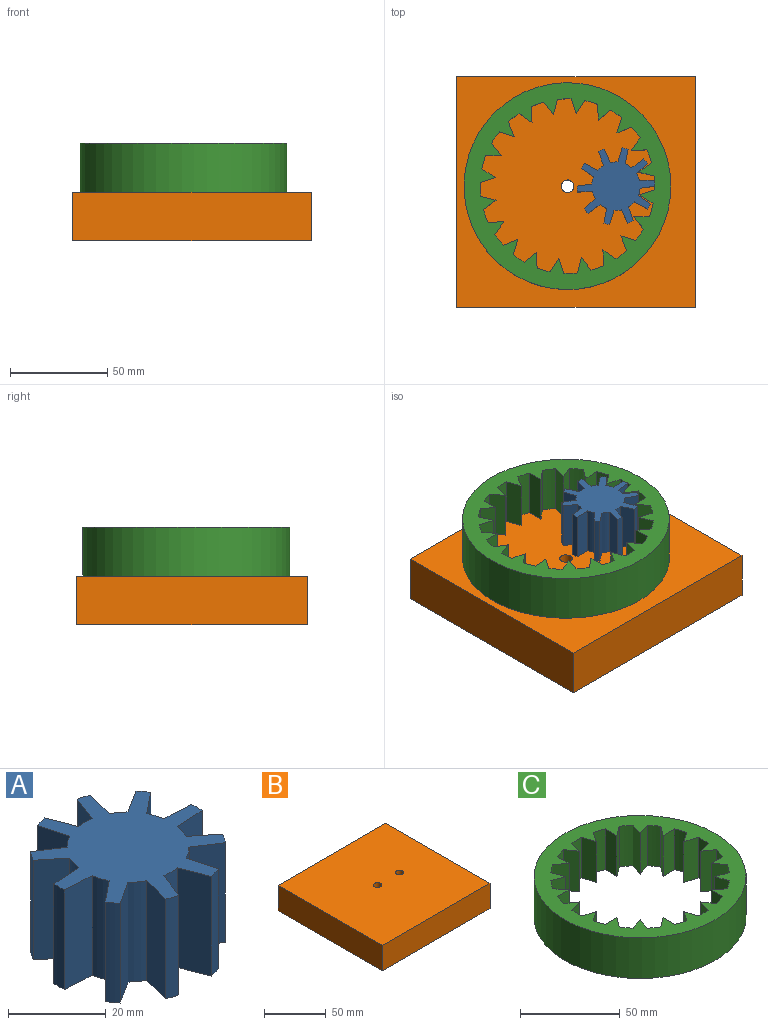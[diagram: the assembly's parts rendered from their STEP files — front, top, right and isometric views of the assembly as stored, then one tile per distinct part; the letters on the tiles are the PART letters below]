
ASSEMBLY  parts=3 mates=2
PART A: 52 faces, bbox 40x38.9x25 mm
  f0: cylinder r=20mm len=25mm, axis (0,0,-1), area 77mm2, adj f3,f4,f5,f6
  f1: cylinder r=12.5mm len=25mm, axis (0,0,-1), area 98.4mm2, adj f2,f3,f4,f5
  f2: plane 25x0.04mm, normal (-0.45,0.89,0), area 1mm2, adj f1,f3,f4,f12
  f3: plane 40x38.88mm, normal (0,0,1), area 752.8mm2, adj f0,f1,f2,f5,f6,f7,f8,f9
  f4: plane 40x38.88mm, normal (0,0,-1), area 752.8mm2, adj f0,f1,f2,f5,f6,f7,f8,f9
  f5: plane 25x7.59mm, normal (0.05,1,0), area 190.1mm2, adj f0,f1,f3,f4
  f6: plane 25x7.63mm, normal (0.05,-1,0), area 191.1mm2, adj f0,f3,f4,f7
  f7: plane 25x0.04mm, normal (0.16,0.99,0), area 1mm2, adj f3,f4,f6,f49
  f8: cylinder r=20mm len=25mm, axis (0,0,-1), area 77mm2, adj f3,f4,f11,f12
  f9: cylinder r=12.5mm len=25mm, axis (0,0,-1), area 98.4mm2, adj f3,f4,f10,f11
  f10: plane 25x0.04mm, normal (-0.89,0.45,0), area 1mm2, adj f3,f4,f9,f17
  f11: plane 25x6.38mm, normal (-0.54,0.84,0), area 190.1mm2, adj f3,f4,f8,f9
  f12: plane 25x5.93mm, normal (0.63,-0.78,0), area 191.1mm2, adj f2,f3,f4,f8
  f13: cylinder r=20mm len=25mm, axis (0,0,-1), area 77mm2, adj f3,f4,f16,f17
  f14: cylinder r=12.5mm len=25mm, axis (0,0,-1), area 98.4mm2, adj f3,f4,f15,f16
  f15: plane 25x0.04mm, normal (-0.99,-0.16,0), area 1mm2, adj f3,f4,f14,f22
  f16: plane 25x7.1mm, normal (-0.93,0.36,0), area 190.1mm2, adj f3,f4,f13,f14
  f17: plane 25x7.39mm, normal (0.97,-0.26,0), area 191.1mm2, adj f3,f4,f10,f13
  f18: cylinder r=20mm len=25mm, axis (0,0,-1), area 77mm2, adj f3,f4,f21,f22
  f19: cylinder r=12.5mm len=25mm, axis (0,0,-1), area 98.4mm2, adj f3,f4,f20,f21
  f20: plane 25x0.03mm, normal (-0.71,-0.71,0), area 1mm2, adj f3,f4,f19,f27
  f21: plane 25x7.35mm, normal (-0.97,-0.26,0), area 190.1mm2, adj f3,f4,f18,f19
  f22: plane 25x7.13mm, normal (0.93,0.36,0), area 191.1mm2, adj f3,f4,f15,f18
  f23: cylinder r=20mm len=25mm, axis (0,0,-1), area 77mm2, adj f3,f4,f26,f27
  f24: cylinder r=12.5mm len=25mm, axis (0,0,-1), area 98.4mm2, adj f3,f4,f25,f26
  f25: plane 25x0.04mm, normal (-0.16,-0.99,0), area 1mm2, adj f3,f4,f24,f32
  f26: plane 25x5.9mm, normal (-0.63,-0.78,0), area 190.1mm2, adj f3,f4,f23,f24
  f27: plane 25x6.42mm, normal (0.54,0.84,0), area 191.1mm2, adj f3,f4,f20,f23
  f28: cylinder r=20mm len=25mm, axis (0,0,-1), area 77mm2, adj f3,f4,f31,f32
  f29: cylinder r=12.5mm len=25mm, axis (0,0,-1), area 98.4mm2, adj f3,f4,f30,f31
  f30: plane 25x0.04mm, normal (0.45,-0.89,0), area 1mm2, adj f3,f4,f29,f37
  f31: plane 25x7.59mm, normal (-0.05,-1,0), area 190.1mm2, adj f3,f4,f28,f29
  f32: plane 25x7.63mm, normal (-0.05,1,0), area 191.1mm2, adj f3,f4,f25,f28
  f33: cylinder r=20mm len=25mm, axis (0,0,-1), area 77mm2, adj f3,f4,f36,f37
  f34: cylinder r=12.5mm len=25mm, axis (0,0,-1), area 98.4mm2, adj f3,f4,f35,f36
  f35: plane 25x0.04mm, normal (0.89,-0.45,0), area 1mm2, adj f3,f4,f34,f42
  f36: plane 25x6.38mm, normal (0.54,-0.84,0), area 190.1mm2, adj f3,f4,f33,f34
  f37: plane 25x5.93mm, normal (-0.63,0.78,0), area 191.1mm2, adj f3,f4,f30,f33
  f38: cylinder r=20mm len=25mm, axis (0,0,-1), area 77mm2, adj f3,f4,f41,f42
  f39: cylinder r=12.5mm len=25mm, axis (0,0,-1), area 98.4mm2, adj f3,f4,f40,f41
  f40: plane 25x0.04mm, normal (0.99,0.16,0), area 1mm2, adj f3,f4,f39,f47
  f41: plane 25x7.1mm, normal (0.93,-0.36,0), area 190.1mm2, adj f3,f4,f38,f39
  f42: plane 25x7.39mm, normal (-0.97,0.26,0), area 191.1mm2, adj f3,f4,f35,f38
  f43: cylinder r=20mm len=25mm, axis (0,0,-1), area 77mm2, adj f3,f4,f46,f47
  f44: cylinder r=12.5mm len=25mm, axis (0,0,-1), area 98.4mm2, adj f3,f4,f45,f46
  f45: plane 25x0.03mm, normal (0.71,0.71,0), area 1mm2, adj f3,f4,f44,f51
  f46: plane 25x7.35mm, normal (0.97,0.26,0), area 190.1mm2, adj f3,f4,f43,f44
  f47: plane 25x7.13mm, normal (-0.93,-0.36,0), area 191.1mm2, adj f3,f4,f40,f43
  f48: cylinder r=20mm len=25mm, axis (0,0,-1), area 77mm2, adj f3,f4,f50,f51
  f49: cylinder r=12.5mm len=25mm, axis (0,0,-1), area 98.4mm2, adj f3,f4,f7,f50
  f50: plane 25x5.9mm, normal (0.63,0.78,0), area 190.1mm2, adj f3,f4,f48,f49
  f51: plane 25x6.42mm, normal (-0.54,-0.84,0), area 191.1mm2, adj f3,f4,f45,f48
PART B: 8 faces, bbox 123.1x118.8x25 mm
  f0: plane 123.12x25mm, normal (0,1,0), area 3078.1mm2, adj f1,f5,f6,f7
  f1: plane 118.81x25mm, normal (-1,0,0), area 2970.3mm2, adj f0,f2,f6,f7
  f2: plane 123.12x25mm, normal (0,-1,0), area 3078.1mm2, adj f1,f5,f6,f7
  f3: cylinder r=3.24mm len=25mm, axis (0,0,1), area 509.5mm2, adj f6,f7
  f4: cylinder r=3.24mm len=25mm, axis (0,0,1), area 509.5mm2, adj f6,f7
  f5: plane 118.81x25mm, normal (1,0,0), area 2970.3mm2, adj f0,f2,f6,f7
  f6: plane 123.12x118.81mm, normal (0,0,-1), area 14562.1mm2, adj f0,f1,f2,f3,f4,f5
  f7: plane 123.12x118.81mm, normal (0,0,1), area 14562.1mm2, adj f0,f1,f2,f3,f4,f5
PART C: 63 faces, bbox 106.6x106.6x25 mm
  f0: cylinder r=45mm len=25mm, axis (0,0,-1), area 176.7mm2, adj f23,f24,f26,f28
  f1: cylinder r=45mm len=25mm, axis (0,0,-1), area 176.7mm2, adj f23,f24,f27,f30
  f2: cylinder r=45mm len=25mm, axis (0,0,-1), area 176.7mm2, adj f23,f24,f29,f32
  f3: cylinder r=45mm len=25mm, axis (0,0,-1), area 176.7mm2, adj f23,f24,f31,f34
  f4: cylinder r=45mm len=25mm, axis (0,0,-1), area 176.7mm2, adj f23,f24,f33,f36
  f5: cylinder r=45mm len=25mm, axis (0,0,-1), area 176.7mm2, adj f23,f24,f35,f38
  f6: cylinder r=45mm len=25mm, axis (0,0,-1), area 176.7mm2, adj f23,f24,f37,f40
  f7: cylinder r=45mm len=25mm, axis (0,0,-1), area 176.7mm2, adj f23,f24,f39,f42
  f8: cylinder r=45mm len=25mm, axis (0,0,-1), area 176.7mm2, adj f23,f24,f41,f44
  f9: cylinder r=45mm len=25mm, axis (0,0,-1), area 176.7mm2, adj f23,f24,f43,f46
  f10: cylinder r=45mm len=25mm, axis (0,0,-1), area 176.7mm2, adj f23,f24,f45,f48
  f11: cylinder r=45mm len=25mm, axis (0,0,-1), area 176.7mm2, adj f23,f24,f47,f50
  f12: cylinder r=45mm len=25mm, axis (0,0,-1), area 176.7mm2, adj f23,f24,f49,f52
  f13: cylinder r=45mm len=25mm, axis (0,0,-1), area 176.7mm2, adj f23,f24,f51,f54
  f14: cylinder r=45mm len=25mm, axis (0,0,-1), area 176.7mm2, adj f23,f24,f53,f56
  f15: cylinder r=45mm len=25mm, axis (0,0,-1), area 176.7mm2, adj f23,f24,f55,f58
  f16: cylinder r=45mm len=25mm, axis (0,0,-1), area 176.7mm2, adj f23,f24,f57,f60
  f17: cylinder r=45mm len=25mm, axis (0,0,-1), area 176.7mm2, adj f23,f24,f59,f62
  f18: cylinder r=45mm len=25mm, axis (0,0,-1), area 176.7mm2, adj f21,f23,f24,f61
  f19: plane 25x6.72mm, normal (-0.57,-0.82,0), area 204.1mm2, adj f20,f21,f23,f24
  f20: cylinder r=45mm len=25mm, axis (0,0,-1), area 176.7mm2, adj f19,f23,f24,f25
  f21: plane 25x7.82mm, normal (-0.29,0.96,0), area 204.1mm2, adj f18,f19,f23,f24
  f22: cylinder r=53.3mm len=106.59mm, axis (0,0,-1), area 8371.8mm2, adj f23,f24
  f23: plane 106.59x106.59mm, normal (0,0,1), area 3094.8mm2, adj f0,f1,f2,f3,f4,f5,f6,f7
  f24: plane 106.59x106.59mm, normal (0,0,-1), area 3094.8mm2, adj f0,f1,f2,f3,f4,f5,f6,f7
  f25: plane 25x8.16mm, normal (0.02,1,0), area 204.1mm2, adj f20,f23,f24,f26
  f26: plane 25x6.49mm, normal (-0.79,-0.61,0), area 204.1mm2, adj f0,f23,f24,f25
  f27: plane 25x7.7mm, normal (-0.94,-0.33,0), area 204.1mm2, adj f1,f23,f24,f28
  f28: plane 25x7.7mm, normal (0.33,0.94,0), area 204.1mm2, adj f0,f23,f24,f27
  f29: plane 25x8.16mm, normal (-1,-0.02,0), area 204.1mm2, adj f2,f23,f24,f30
  f30: plane 25x6.49mm, normal (0.61,0.79,0), area 204.1mm2, adj f1,f23,f24,f29
  f31: plane 25x7.82mm, normal (-0.96,0.29,0), area 204.1mm2, adj f3,f23,f24,f32
  f32: plane 25x6.72mm, normal (0.82,0.57,0), area 204.1mm2, adj f2,f23,f24,f31
  f33: plane 25x6.72mm, normal (-0.82,0.57,0), area 204.1mm2, adj f4,f23,f24,f34
  f34: plane 25x7.82mm, normal (0.96,0.29,0), area 204.1mm2, adj f3,f23,f24,f33
  f35: plane 25x6.49mm, normal (-0.61,0.79,0), area 204.1mm2, adj f5,f23,f24,f36
  f36: plane 25x8.16mm, normal (1,-0.02,0), area 204.1mm2, adj f4,f23,f24,f35
  f37: plane 25x7.7mm, normal (-0.33,0.94,0), area 204.1mm2, adj f6,f23,f24,f38
  f38: plane 25x7.7mm, normal (0.94,-0.33,0), area 204.1mm2, adj f5,f23,f24,f37
  f39: plane 25x8.16mm, normal (-0.02,1,0), area 204.1mm2, adj f7,f23,f24,f40
  f40: plane 25x6.49mm, normal (0.79,-0.61,0), area 204.1mm2, adj f6,f23,f24,f39
  f41: plane 25x7.82mm, normal (0.29,0.96,0), area 204.1mm2, adj f8,f23,f24,f42
  f42: plane 25x6.72mm, normal (0.57,-0.82,0), area 204.1mm2, adj f7,f23,f24,f41
  f43: plane 25x6.72mm, normal (0.57,0.82,0), area 204.1mm2, adj f9,f23,f24,f44
  f44: plane 25x7.82mm, normal (0.29,-0.96,0), area 204.1mm2, adj f8,f23,f24,f43
  f45: plane 25x6.49mm, normal (0.79,0.61,0), area 204.1mm2, adj f10,f23,f24,f46
  f46: plane 25x8.16mm, normal (-0.02,-1,0), area 204.1mm2, adj f9,f23,f24,f45
  f47: plane 25x7.7mm, normal (0.94,0.33,0), area 204.1mm2, adj f11,f23,f24,f48
  f48: plane 25x7.7mm, normal (-0.33,-0.94,0), area 204.1mm2, adj f10,f23,f24,f47
  f49: plane 25x8.16mm, normal (1,0.02,0), area 204.1mm2, adj f12,f23,f24,f50
  f50: plane 25x6.49mm, normal (-0.61,-0.79,0), area 204.1mm2, adj f11,f23,f24,f49
  f51: plane 25x7.82mm, normal (0.96,-0.29,0), area 204.1mm2, adj f13,f23,f24,f52
  f52: plane 25x6.72mm, normal (-0.82,-0.57,0), area 204.1mm2, adj f12,f23,f24,f51
  f53: plane 25x6.72mm, normal (0.82,-0.57,0), area 204.1mm2, adj f14,f23,f24,f54
  f54: plane 25x7.82mm, normal (-0.96,-0.29,0), area 204.1mm2, adj f13,f23,f24,f53
  f55: plane 25x6.49mm, normal (0.61,-0.79,0), area 204.1mm2, adj f15,f23,f24,f56
  f56: plane 25x8.16mm, normal (-1,0.02,0), area 204.1mm2, adj f14,f23,f24,f55
  f57: plane 25x7.7mm, normal (0.33,-0.94,0), area 204.1mm2, adj f16,f23,f24,f58
  f58: plane 25x7.7mm, normal (-0.94,0.33,0), area 204.1mm2, adj f15,f23,f24,f57
  f59: plane 25x8.16mm, normal (0.02,-1,0), area 204.1mm2, adj f17,f23,f24,f60
  f60: plane 25x6.49mm, normal (-0.79,0.61,0), area 204.1mm2, adj f16,f23,f24,f59
  f61: plane 25x7.82mm, normal (-0.29,-0.96,0), area 204.1mm2, adj f18,f23,f24,f62
  f62: plane 25x6.72mm, normal (-0.57,0.82,0), area 204.1mm2, adj f17,f23,f24,f61
PLACE A rot(axis=(0,0,-1),139.8deg) t=(20.63,2.96,25)mm
PLACE B t=(20.63,2.96,25)mm
PLACE C rot(axis=(0,0,-1),69.9deg) t=(4.23,-20.52,25)mm
MATE revolute C.f22 <-> B.f3  axis (0,0,-1) through (-4.37,2.96,25)mm
MATE revolute A.f49 <-> B.f4  axis (0,0,-1) through (20.63,2.96,25)mm
